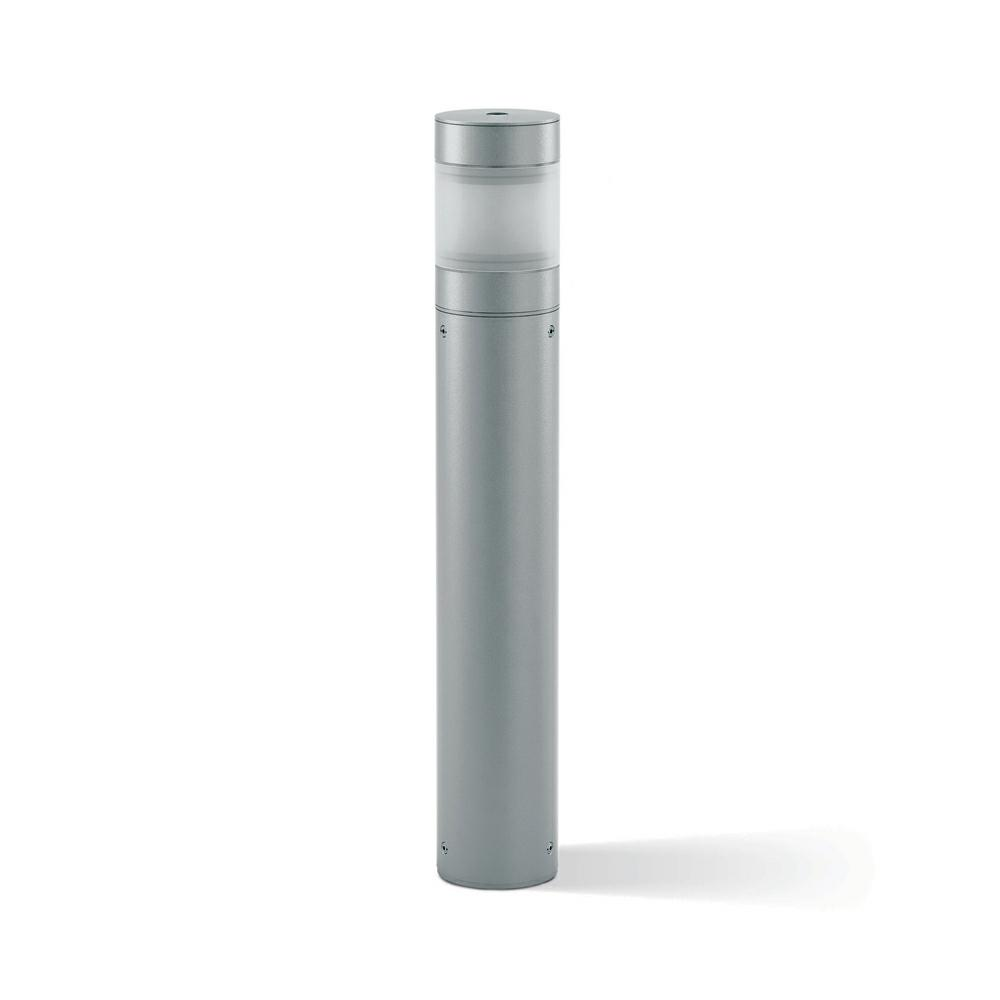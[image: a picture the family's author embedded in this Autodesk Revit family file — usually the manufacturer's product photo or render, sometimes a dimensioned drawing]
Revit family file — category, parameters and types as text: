
# Revit family: Platek_Tube
name_source: partatom
category: Apparecchi per illuminazione
revit_build: Autodesk Revit 2017 (Build: 20160225_1515(x64)
units: mm (PartAtom-declared; Revit-internal decimal feet)

## family parameters
Basato su piano di lavoro = No
Condiviso = No
Punto di calcolo locali = No
Quota connettore circolare = Usa diametro
Sempre verticale = Sì
Sorgente d'illuminazione = Sì
Taglio con vuoti quando caricato = No
Tipo di parte = Normale

## types (8) — shared parameters
Aluminium = PLK_Light Source
Angolo inclinazione = 90.00°
BASE = 75 mm
Beam Angle = 0.00°
Body = PLK_Grey
CRI = >80
Carico apparente = 0 VA
Colour Temperature = 3000 K
Depth = 150 mm
Descrizione = Outdoor Lighting, Floor/Ground Illumination
Diffuse Type = PMMA
Dimmable = No
Emetti da diametro cerchio = 150 mm
Energy Efficiency Rating = A/A+/A++
Filtro dei colori = 16777215
Frequency = 0/50/60 Hz
IK Rating = IK 10
IP Rating = IP65
Insulation Class = 2
LED Protection = Surge protection included
Lampada = LED
Light Source = PLK_Light Source
Modello = Tube
Mounting Type = Ground
Nota chiave = Other Led colors available on request
PLATEK FInishes = Painted Aluminium Avalaible in Anthracite/Black/White/Corten/Bronze
Power Supply Unit = Included
Product Documentation Link = http://www.platek.eu
Product Page URL = http://www.platek.eu
Produttore = PLATEK SRL
Rendi la forma visibile nel rendering = No
Supply Voltage = 230 V
Supply Voltage Max = 240 V
Supply Voltage Min = 220 V
URL = www.platek.eu
Variazione temperatura colore lampada con luminosità attenuata = <Nessuno>
Width = 150 mm

## per-type parameters (varying)
| type | Codice assieme | Commenti sul tipo | File diagramma fotometrico | H Body1000 | H Body260 | H Body3000 | H Body4000 | H Light1000 | H Light260 | H Light3000 | H Light4000 | Height Body | Height Light | Immagine tipo | Luminaire Luminous Flux | Luminaire Luminous Intensity | Luminaire Wattage | Manufacturer Comment | PLATEK Article Code | Product Dimension |
| 3365610_10W_LED_3000K_H260mm | 3365610.06(Grey); 3365610.08(Anthracite); 3365610.01(Black); 3365610.02(White); 3365610.07(Corten); 3365610.09(Bronze) | Pedestrian areas, Urban zones, Paths, Roads | 3365610.IES | No | Sì | No | No | No | Sì | No | No | 14 mm  [stored 0.0459318 ft] | 246 mm  [stored 0.807087 ft] | tube_260_trasparente.jpg | 416 lm | 107 cd | 10 W | Transparent | 3365610 | D160mm x H260mm |
| 3365611_20W_LED_3000K_H1000mm | 3365611.06(Grey); 3365611.08(Anthracite);3365611.01(Black); 3365611.02(White); 3365611.07(Corten); 3365611.09(Bronze) | Pedestrian areas, Urban zones, Paths, Roads | 3365611.IES | Sì | No | No | No | Sì | No | No | No | 750 mm  [stored 2.46063 ft] | 250 mm  [stored 0.82021 ft] | tube_1000_trasparente.jpg | 924 lm | 238 cd | 20 W |  | 3365611 | D160mm x H1000mm |
| 3365613_42W_LED_3000K_H3000mm | 3365613.06(Grey); 3365613.08(Anthracite); 3365613.01(Black); 3365613.02(White); 3365613.07(Corten); 3365613.09(Bronze) | Pedestrian areas, Urban zones, Paths, Roads | 3365613.IES | No | No | Sì | No | No | No | Sì | No | 2000 mm  [stored 6.56168 ft] | 1000 mm  [stored 3.28084 ft] | tube_3000_trasparente.jpg | 2015 lm | 558 cd | 42 W |  | 3365613 | D160mm x H3000mm |
| 3365614_42W_LED_3000K_H4000mm | 3365614.06(Grey); 3365614.08(Anthracite); 3365614.01(Black); 3365614.02(White); 3365614.07(Corten); 3365614.09(Bronze) | Siutable for restaurants, balconies, terraces, lounge areas | 3365614.IES | No | No | No | Sì | No | No | No | Sì | 2000 mm  [stored 6.56168 ft] | 2000 mm  [stored 6.56168 ft] | tube_4000_trasparente.jpg | 2015 lm | 558 cd | 42 W |  | 3365614 | D160mm x H4000mm |
| 3366610_10W_LED_3000K_H260mm | 3366610.06(Grey); 3366610.08(Anthracite); 3366610.01(Black); 3366610.02(White); 3366610.07(Corten); 3366610.09(Bronze) | Pedestrian areas, Urban zones, Paths, Roads | 3366610.IES | No | Sì | No | No | No | Sì | No | No | 14 mm  [stored 0.0459318 ft] | 246 mm  [stored 0.807087 ft] | tube_260_sabbiato.jpg | 607 lm | 918 cd | 10 W | Sandblasted | 3366610 | D160mm x H260mm |
| 3366611_20W_LED_3000K_H1000mm | 3366611.06(Grey); 3366611.08(Anthracite);3366611.01(Black); 3365611.02(White); 3366611.07(Corten); 3366611.09(Bronze) | Pedestrian areas, Urban zones, Paths, Roads | 3366611.IES | Sì | No | No | No | Sì | No | No | No | 750 mm  [stored 2.46063 ft] | 250 mm  [stored 0.82021 ft] | tube_1000_sabbiato.jpg | 1250 lm | 189 cd | 20 W | Sandblasted | 3366611 | D160mm x H1000mm |
| 3366613_42W_LED_3000K_H3000mm | 3366613.06(Grey); 3366613.08(Anthracite); 3366613.01(Black); 3366613.02(White); 3366613.07(Corten); 3366613.09(Bronze) | Pedestrian areas, Urban zones, Paths, Roads | 3366613.IES | No | No | Sì | No | No | No | Sì | No | 2000 mm  [stored 6.56168 ft] | 1000 mm  [stored 3.28084 ft] | tube_3000_sabbiato.jpg | 2835 lm | 429 cd | 42 W | Sandblasted | 3366613 | D160mm x H3000mm |
| 3366614_42W_LED_3000K_H4000mm | 3366614.06(Grey); 3366614.08(Anthracite); 3366614.01(Black); 3366614.02(White); 3366614.07(Corten); 3366614.09(Bronze) | Siutable for restaurants, balconies, terraces, lounge areas | 3366614.IES | No | No | No | Sì | No | No | No | Sì | 2000 mm  [stored 6.56168 ft] | 2000 mm  [stored 6.56168 ft] | tube_4000_sabbiato.jpg | 2835 lm | 429 cd | 42 W | Sandblasted | 3366614 | D160mm x H4000mm |

note: [stored X ft] marks values corroborated as IEEE doubles in the binary element streams (Revit-internal decimal feet)
